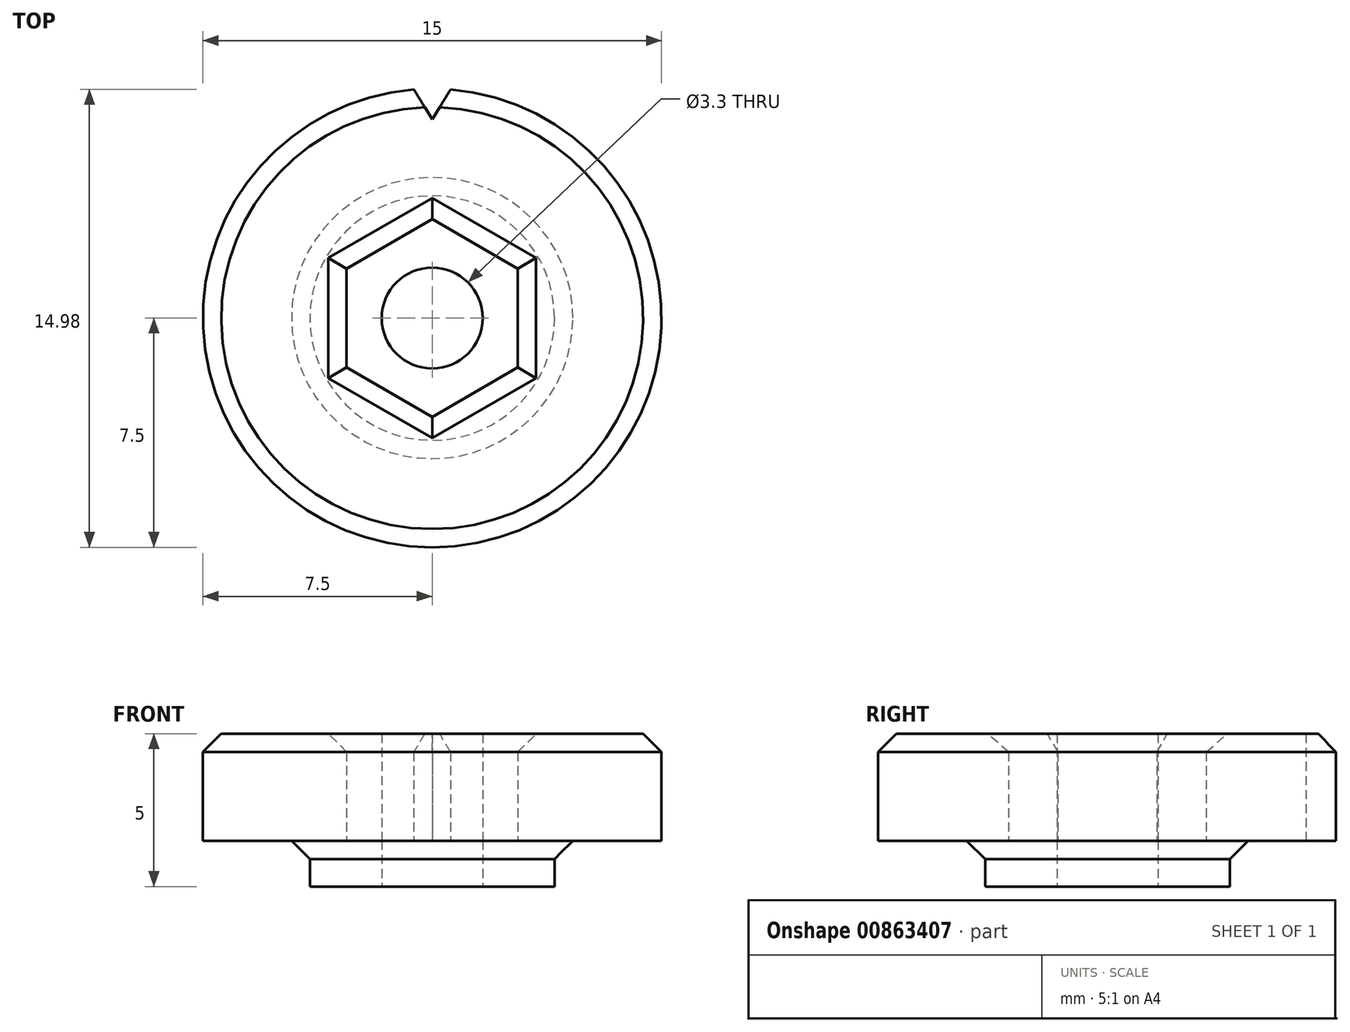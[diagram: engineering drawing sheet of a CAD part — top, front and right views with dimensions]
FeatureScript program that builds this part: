
annotation { "Feature Type Name" : "Feature", "Feature Type Description" : "" }
export const myFeature = defineFeature(function(context is Context, id is Id, definition is map)
    precondition{}
    {
        {
            var Q0;
            Q0=qCreatedBy(makeId("Top.planeOp"),FACE);
            var sketch = newSketch(context, id + "F0", { "sketchPlane" : qUnion([Q0])});
            skCircle(sketch, "E0", {"center": v(0, 0) * mm, "radius": 7.5 * mm});
            skCircle(sketch, "E1.cCircle", {"center": v(0, 0) * mm, "radius": 2.8 * mm, "construction": true});
            skLineSegment(sketch, "E1.0", {"start": v(-2.8, -1.62) * mm, "end": v(-2.8, 1.62) * mm});
            skLineSegment(sketch, "E1.1", {"start": v(-2.8, 1.62) * mm, "end": v(0, 3.23) * mm});
            skLineSegment(sketch, "E1.2", {"start": v(0, 3.23) * mm, "end": v(2.8, 1.62) * mm});
            skLineSegment(sketch, "E1.3", {"start": v(2.8, 1.62) * mm, "end": v(2.8, -1.62) * mm});
            skLineSegment(sketch, "E1.4", {"start": v(2.8, -1.62) * mm, "end": v(0, -3.23) * mm});
            skLineSegment(sketch, "E1.5", {"start": v(0, -3.23) * mm, "end": v(-2.8, -1.62) * mm});
            skPoint(sketch, "E1.0.midPoint", {"position": v(-2.8, 0) * mm});
            skLineSegment(sketch, "E2", {"start": v(-0.6, 7.48) * mm, "end": v(0, 6.5) * mm});
            skLineSegment(sketch, "E3", {"start": v(0, 6.5) * mm, "end": v(0.6, 7.48) * mm});
            skCircle(sketch, "E4", {"center": v(0, 0) * mm, "radius": 4 * mm});
            skCircle(sketch, "E5", {"center": v(0, 0) * mm, "radius": 1.65 * mm});
            skSolve(sketch);
        }
        {
            var Q0;
            {var subQ0=sQuery(id+"F0.wireOp",EDGE,"E2");Q0=makeQuery(id+"F0.imprint","IMPRINT",FACE,{"disambiguationData":[TD([[makeQuery(id+"F0.imprint","IMPRINT",EDGE,{"derivedFrom":subQ0}),1.0]])]});}
            var Q1;
            Q1=makeQuery(id+"F0.imprint","IMPRINT",FACE,{"disambiguationData":[TD([[makeQuery(id+"F0.imprint","IMPRINT",EDGE,{"derivedFrom":sQuery(id+"F0.wireOp",EDGE,"E1.0")}),1.0]])]});
            var Q2;
            {var subQ0=sQuery(id+"F0.wireOp",EDGE,"E2");Q2=makeQuery(id+"F0.imprint","IMPRINT",FACE,{"disambiguationData":[TD([[makeQuery(id+"F0.imprint","IMPRINT",EDGE,{"derivedFrom":subQ0}),-1.0]])]});}
            extrude(context, id + "F1", {"entities" : qUnion([Q0, Q1, Q2]), "depth" : 5 * mm, "offsetDistance" : 25 * mm});
        }
        {
            var Q0;
            {var subQ0=sQuery(id+"F0.wireOp",EDGE,"E2");Q0=makeQuery(id+"F0.imprint","IMPRINT",FACE,{"disambiguationData":[TD([[makeQuery(id+"F0.imprint","IMPRINT",EDGE,{"derivedFrom":subQ0}),-1.0]])]});}
            var Q1;
            {var subQ0=sQuery(id+"F0.wireOp",EDGE,"E2");Q1=makeQuery(id+"F0.imprint","IMPRINT",FACE,{"disambiguationData":[TD([[makeQuery(id+"F0.imprint","IMPRINT",EDGE,{"derivedFrom":subQ0}),1.0]])]});}
            extrude(context, id + "F2", {"entities" : qUnion([Q0, Q1]), "operationType" : NewBodyOperationType.REMOVE, "depth" : 1.5 * mm, "offsetDistance" : 25 * mm});
        }
        {
            var Q0;
            Q0=makeQuery(id+"F0.imprint","IMPRINT",FACE,{"disambiguationData":[TD([[makeQuery(id+"F0.imprint","IMPRINT",EDGE,{"derivedFrom":sQuery(id+"F0.wireOp",EDGE,"E1.0")}),-1.0]])]});
            extrude(context, id + "F3", {"entities" : qUnion([Q0]), "operationType" : NewBodyOperationType.ADD, "depth" : 1.5 * mm, "offsetDistance" : 25 * mm});
        }
        {
            var Q0;
            Q0=makeQuery(id+"F2.boolean.opBoolean","COPY",EDGE,{"derivedFrom":makeQuery(id+"F2.opExtrude","CAP_EDGE",EDGE,{"disambiguationData":[OSD([sQuery(id+"F0.wireOp",EDGE,"E0")])],"isStart":false})});
            var Q1;
            Q1=makeQuery(id+"F1.opExtrude","CAP_EDGE",EDGE,{"disambiguationData":[OSD([sQuery(id+"F0.wireOp",EDGE,"E0")])],"isStart":false});
            var Q2;
            Q2=makeQuery(id+"F2.boolean.opBoolean","COPY",EDGE,{"derivedFrom":makeQuery(id+"F2.opExtrude","CAP_EDGE",EDGE,{"disambiguationData":[OSD([sQuery(id+"F0.wireOp",EDGE,"E4")])],"isStart":false})});
            var Q3;
            Q3=makeQuery(id+"F2.boolean.opBoolean","COPY",EDGE,{"derivedFrom":makeQuery(id+"F2.opExtrude","CAP_EDGE",EDGE,{"disambiguationData":[OSD([sQuery(id+"F0.wireOp",EDGE,"E4")])],"isStart":true})});
            var Q4;
            Q4=makeQuery(id+"F1.opExtrude","CAP_EDGE",EDGE,{"disambiguationData":[OSD([sQuery(id+"F0.wireOp",EDGE,"E1.1")])],"isStart":false});
            var Q5;
            Q5=makeQuery(id+"F1.opExtrude","CAP_EDGE",EDGE,{"disambiguationData":[OSD([sQuery(id+"F0.wireOp",EDGE,"E1.0")])],"isStart":false});
            var Q6;
            Q6=makeQuery(id+"F1.opExtrude","CAP_EDGE",EDGE,{"disambiguationData":[OSD([sQuery(id+"F0.wireOp",EDGE,"E1.5")])],"isStart":false});
            var Q7;
            Q7=makeQuery(id+"F1.opExtrude","CAP_EDGE",EDGE,{"disambiguationData":[OSD([sQuery(id+"F0.wireOp",EDGE,"E1.4")])],"isStart":false});
            var Q8;
            Q8=makeQuery(id+"F1.opExtrude","CAP_EDGE",EDGE,{"disambiguationData":[OSD([sQuery(id+"F0.wireOp",EDGE,"E1.3")])],"isStart":false});
            var Q9;
            Q9=makeQuery(id+"F1.opExtrude","CAP_EDGE",EDGE,{"disambiguationData":[OSD([sQuery(id+"F0.wireOp",EDGE,"E1.2")])],"isStart":false});
            chamfer(context, id + "F4", {"entities" : qUnion([Q0, Q1, Q2, Q3, Q4, Q5, Q6, Q7, Q8, Q9]), "width" : .6 * mm, "tangentPropagation" : true});
        }
        {
            var Q0;
            {var subQ0=sQuery(id+"F0.wireOp",EDGE,"E2");Q0=makeQuery(id+"F0.imprint","IMPRINT",FACE,{"disambiguationData":[TD([[makeQuery(id+"F0.imprint","IMPRINT",EDGE,{"derivedFrom":subQ0}),1.0]])]});}
            var Q1;
            Q1=makeQuery(id+"F1.opExtrude","CAP_FACE",FACE,{"disambiguationData":[OSD([sQuery(id+"F0.wireOp",EDGE,"E0"),sQuery(id+"F0.wireOp",EDGE,"E1.0"),sQuery(id+"F0.wireOp",EDGE,"E1.1"),sQuery(id+"F0.wireOp",EDGE,"E1.2"),sQuery(id+"F0.wireOp",EDGE,"E1.3"),sQuery(id+"F0.wireOp",EDGE,"E1.4"),sQuery(id+"F0.wireOp",EDGE,"E1.5")])],"isStart":false});
            extrude(context, id + "F5", {"entities" : qUnion([Q0]), "operationType" : NewBodyOperationType.REMOVE, "endBound" : BoundingType.UP_TO_SURFACE, "depth" : 25 * mm, "endBoundEntityFace" : qUnion([Q1]), "offsetDistance" : 25 * mm});
        }
        {
            var Q0;
            Q0=makeQuery(id+"F3.opExtrude","CAP_FACE",FACE,{"disambiguationData":[OSD([sQuery(id+"F0.wireOp",EDGE,"E1.0"),sQuery(id+"F0.wireOp",EDGE,"E1.1"),sQuery(id+"F0.wireOp",EDGE,"E1.2"),sQuery(id+"F0.wireOp",EDGE,"E1.3"),sQuery(id+"F0.wireOp",EDGE,"E1.4"),sQuery(id+"F0.wireOp",EDGE,"E1.5"),sQuery(id+"F0.wireOp",EDGE,"E5")])],"isStart":false});
            var sketch = newSketch(context, id + "F6", { "sketchPlane" : qUnion([Q0])});
            skCircle(sketch, "E6.0", {"center": v(0, 0) * mm, "radius": 1.65 * mm});
            skSolve(sketch);
        }
        {
            var Q0;
            Q0 = qSketchRegion(id + "F6", true);
            var Q1;
            Q1=makeQuery(id+"F1.opExtrude","CAP_FACE",FACE,{"disambiguationData":[OSD([sQuery(id+"F0.wireOp",EDGE,"E0"),sQuery(id+"F0.wireOp",EDGE,"E1.0"),sQuery(id+"F0.wireOp",EDGE,"E1.1"),sQuery(id+"F0.wireOp",EDGE,"E1.2"),sQuery(id+"F0.wireOp",EDGE,"E1.3"),sQuery(id+"F0.wireOp",EDGE,"E1.4"),sQuery(id+"F0.wireOp",EDGE,"E1.5")])],"isStart":false});
            extrude(context, id + "F7", {"entities" : qUnion([Q0]), "operationType" : NewBodyOperationType.ADD, "endBound" : BoundingType.UP_TO_SURFACE, "depth" : 25 * mm, "endBoundEntityFace" : qUnion([Q1]), "offsetDistance" : 25 * mm});
        }
    });
